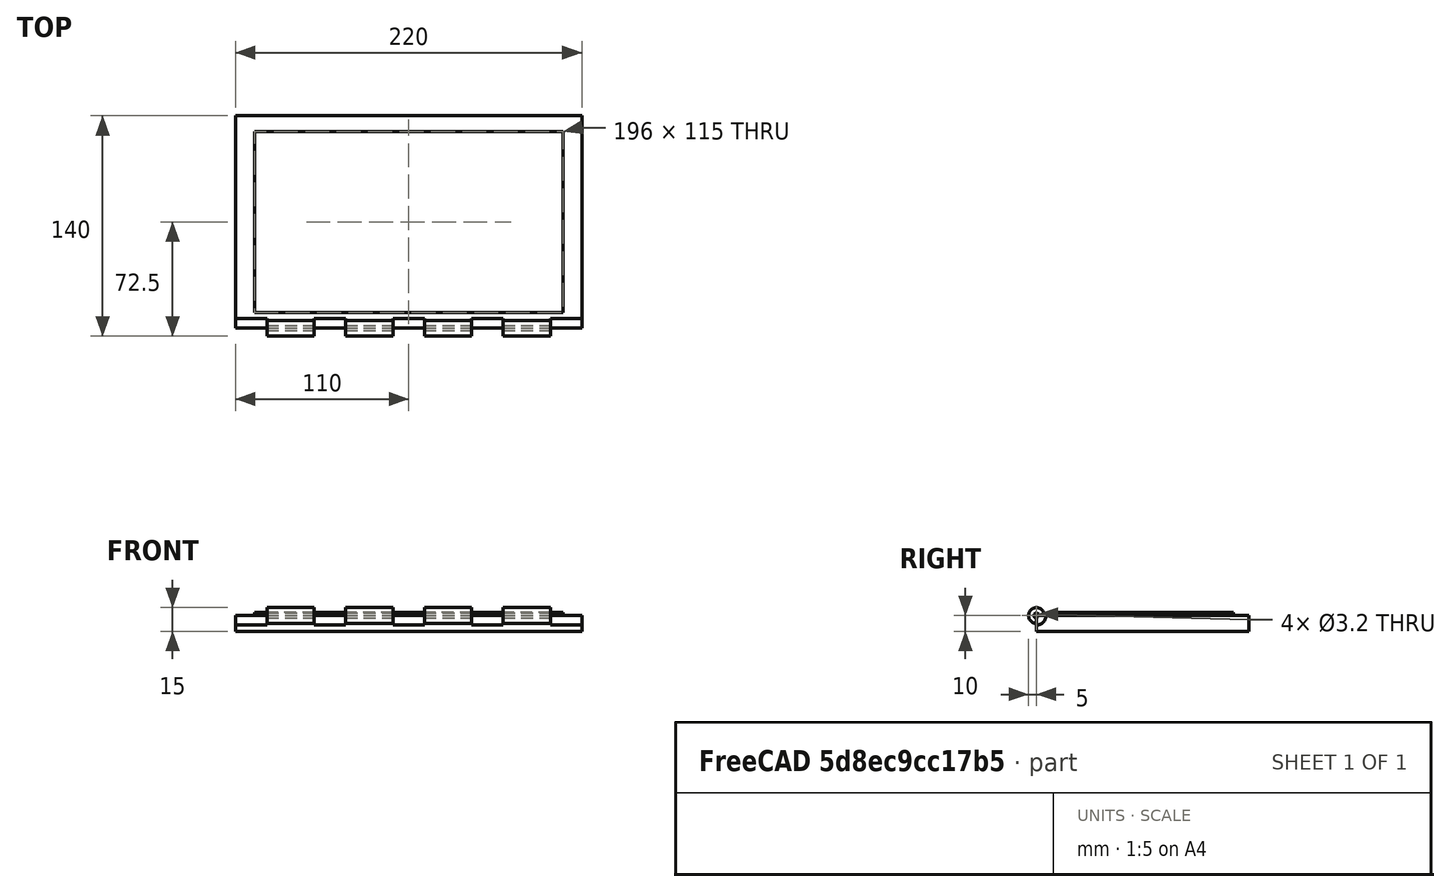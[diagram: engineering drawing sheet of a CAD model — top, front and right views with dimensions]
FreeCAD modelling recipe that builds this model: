
FCSTD DOCUMENT  (FreeCAD 0.19R)
Label: SwitchCaseSmallRLid
License: All rights reserved
LicenseURL: http://en.wikipedia.org/wiki/All_rights_reserved
objects: Part::Cylinder×10, Sketcher::SketchObject×2, PartDesign::Pad×2, Part::MultiFuse×2, Part::Cut×2, PartDesign::Body×1
note: 21 computed .brp shape members not serialized (recipe doc carries the construction recipe); baked Part::Feature solids carry a one-line shape summary decoded from their .brp

FEATURE [Sketcher::SketchObject] Sketch
  FullyConstrained = true
  MapMode = 5
  Support = -> [XY_Plane]
  sketch-geometry (4):
    g0: LineSegment StartX=-110 StartY=67.5 StartZ=0 EndX=110 EndY=67.5 EndZ=0
    g1: LineSegment StartX=110 StartY=67.5 StartZ=0 EndX=110 EndY=-67.5 EndZ=0
    g2: LineSegment StartX=110 StartY=-67.5 StartZ=0 EndX=-110 EndY=-67.5 EndZ=0
    g3: LineSegment StartX=-110 StartY=-67.5 StartZ=0 EndX=-110 EndY=67.5 EndZ=0
  constraints (11):
    c: Coincident(g0,g1)
    c: Coincident(g1,g2)
    c: Coincident(g2,g3)
    c: Coincident(g3,g0)
    c: Horizontal(g0)
    c: Horizontal(g2)
    c: Vertical(g1)
    c: Vertical(g3)
    c: Symmetric(g0,g2,g-1)
    c: Distance(g0) = 220
    c: Distance(g1) = 135
FEATURE [PartDesign::Pad] Pad
  Direction = (1,1,1)
  Length = 10
  Length2 = 100
  Profile = -> Sketch
  Type = 0
FEATURE [Sketcher::SketchObject] Sketch001
  FullyConstrained = true
  MapMode = 5
  Placement = pos=(0,0,10) rot=(0,0,1;0rad)
  Support = -> [Pad]
  sketch-geometry (4):
    g0: LineSegment StartX=-98 StartY=57.5 StartZ=0 EndX=98 EndY=57.5 EndZ=0
    g1: LineSegment StartX=98 StartY=57.5 StartZ=0 EndX=98 EndY=-57.5 EndZ=0
    g2: LineSegment StartX=98 StartY=-57.5 StartZ=0 EndX=-98 EndY=-57.5 EndZ=0
    g3: LineSegment StartX=-98 StartY=-57.5 StartZ=0 EndX=-98 EndY=57.5 EndZ=0
  constraints (11):
    c: Coincident(g0,g1)
    c: Coincident(g1,g2)
    c: Coincident(g2,g3)
    c: Coincident(g3,g0)
    c: Horizontal(g0)
    c: Horizontal(g2)
    c: Vertical(g1)
    c: Vertical(g3)
    c: Distance(g0) = 196
    c: Distance(g1) = 115
    c: Symmetric(g0,g2,g-1)
FEATURE [PartDesign::Pad] Pad001
  BaseFeature = -> Pad
  Direction = (1,1,1)
  Length = 2
  Length2 = 100
  Profile = -> Sketch001
  Type = 0
FEATURE [PartDesign::Body] Body
  Group = -> [Sketch,Pad,Sketch001,Pad001]
  Origin = -> Origin
  Tip = -> Pad001
FEATURE [Part::Cylinder] Cylinder
  Angle = 360
  AttacherType = Attacher::AttachEngine3D
  Height = 30
  Placement = pos=(60,-67.5,10) rot=(0,1,0;1.5708rad)
  Radius = 5
FEATURE [Part::Cylinder] Cylinder001
  Angle = 360
  AttacherType = Attacher::AttachEngine3D
  Height = 30
  Placement = pos=(10,-67.5,10) rot=(0,1,0;1.5708rad)
  Radius = 5
FEATURE [Part::Cylinder] Cylinder002
  Angle = 360
  AttacherType = Attacher::AttachEngine3D
  Height = 30
  Placement = pos=(-40,-67.5,10) rot=(0,1,0;1.5708rad)
  Radius = 5
FEATURE [Part::Cylinder] Cylinder003
  Angle = 360
  AttacherType = Attacher::AttachEngine3D
  Height = 30
  Placement = pos=(-90,-67.5,10) rot=(0,1,0;1.5708rad)
  Radius = 5
FEATURE [Part::Cylinder] Cylinder004 .. Cylinder008  x5 (patterned run collapsed; names and placements below)
  Angle = 360
  AttacherType = Attacher::AttachEngine3D
  Height = 20
  Radius = 6
  placements: 5 in arithmetic series — first pos=(90,-67.5,10) rot=(0,1,0;1.5708rad), step (-50,0,0), last pos=(-110,-67.5,10) rot=(0,1,0;1.5708rad)
FEATURE [Part::MultiFuse] Fusion
  Shapes = -> [Cylinder004,Cylinder005,Cylinder006,Cylinder007,Cylinder008]
FEATURE [Part::Cut] Cut
  Base = -> Pad001
  Tool = -> Fusion
FEATURE [Part::MultiFuse] Fusion001
  Shapes = -> [Cylinder003,Cylinder002,Cylinder001,Cylinder,Cut]
FEATURE [Part::Cylinder] Cylinder009
  Angle = 360
  AttacherType = Attacher::AttachEngine3D
  Height = 220
  Placement = pos=(-110,-67.5,10) rot=(0,1,0;1.5708rad)
  Radius = 1.6
FEATURE [Part::Cut] Cut001
  Base = -> Fusion001
  Tool = -> Cylinder009
